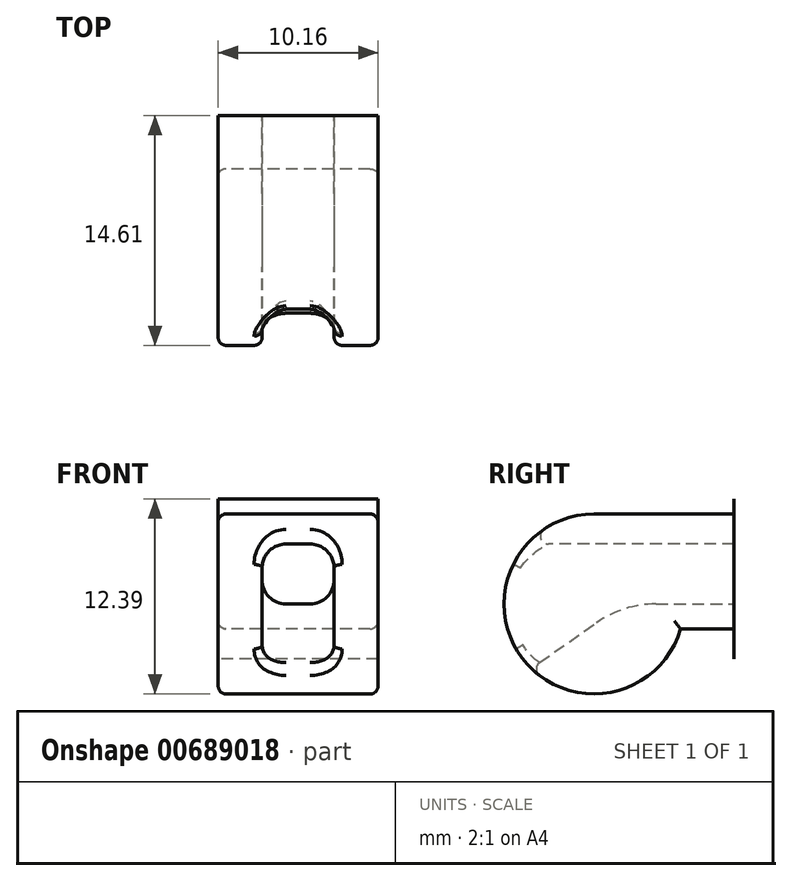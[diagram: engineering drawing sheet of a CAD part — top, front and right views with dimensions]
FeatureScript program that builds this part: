
annotation { "Feature Type Name" : "Feature", "Feature Type Description" : "" }
export const myFeature = defineFeature(function(context is Context, id is Id, definition is map)
    precondition{}
    {
        {
            var Q0;
            Q0=qCreatedBy(makeId("Front.planeOp"),FACE);
            var sketch = newSketch(context, id + "F0", { "sketchPlane" : qUnion([Q0])});
            skLineSegment(sketch, "E0.bottom", {"start": v(10.16, 8.26) * mm, "end": v(-10.16, 8.26) * mm});
            skLineSegment(sketch, "E0.top", {"start": v(10.16, -8.26) * mm, "end": v(-10.16, -8.26) * mm});
            skLineSegment(sketch, "E0.left", {"start": v(10.16, 8.26) * mm, "end": v(10.16, -8.26) * mm});
            skLineSegment(sketch, "E0.right", {"start": v(-10.16, 8.26) * mm, "end": v(-10.16, -8.26) * mm});
            skPoint(sketch, "E0.middle", {"position": v(0, 0) * mm});
            skSolve(sketch);
        }
        {
            var Q0;
            Q0=qCreatedBy(makeId("Right.planeOp"),FACE);
            var sketch = newSketch(context, id + "F1", { "sketchPlane" : qUnion([Q0])});
            skCircle(sketch, "E1", {"center": v(-8.9, 0) * mm, "radius": 5.72 * mm});
            skLineSegment(sketch, "E2", {"start": v(-8.9, 5.72) * mm, "end": v(0, 5.72) * mm});
            skLineSegment(sketch, "E3", {"start": v(-3.4, -1.59) * mm, "end": v(0, -1.59) * mm});
            skPoint(sketch, "E4.0", {"position": v(0, 8.26) * mm});
            skPoint(sketch, "E5.0", {"position": v(0, -8.26) * mm});
            skLineSegment(sketch, "E6.0", {"start": v(0, 8.26) * mm, "end": v(0, -8.26) * mm});
            skPoint(sketch, "E7", {"position": v(0, 0) * mm});
            skSolve(sketch);
        }
        {
            var Q0;
            Q0=qSketchRegion(id+"F1",true);
            extrude(context, id + "F2", {"entities" : qUnion([Q0]), "endBound" : BoundingType.SYMMETRIC, "depth" : 10.16 * mm, "offsetDistance" : 25.4 * mm});
        }
        {
            var Q0;
            Q0=makeQuery(id+"F2.opExtrude","SWEPT_FACE",FACE,{"disambiguationData":[OSD([sQuery(id+"F1.wireOp",EDGE,"E6.0")])]});
            var sketch = newSketch(context, id + "F3", { "sketchPlane" : qUnion([Q0])});
            skLineSegment(sketch, "E8.bottom", {"start": v(-5.08, 5.72) * mm, "end": v(5.08, 5.72) * mm});
            skLineSegment(sketch, "E8.top", {"start": v(-5.08, -1.59) * mm, "end": v(5.08, -1.59) * mm});
            skLineSegment(sketch, "E8.left", {"start": v(-5.08, 5.72) * mm, "end": v(-5.08, -1.59) * mm});
            skLineSegment(sketch, "E8.right", {"start": v(5.08, 5.72) * mm, "end": v(5.08, -1.59) * mm});
            skSolve(sketch);
        }
        {
            var Q0;
            Q0 = qSketchRegion(id + "F3", true);
            extrude(context, id + "F4", {"entities" : qUnion([Q0]), "operationType" : NewBodyOperationType.ADD, "depth" : 1 / 406.4 * mm, "offsetDistance" : 25.4 * mm});
        }
        {
            var Q0;
            Q0=makeQuery(id+"F4.opExtrude","CAP_FACE",FACE,{"disambiguationData":[OSD([sQuery(id+"F3.wireOp",EDGE,"E8.bottom"),sQuery(id+"F3.wireOp",EDGE,"E8.top"),sQuery(id+"F3.wireOp",EDGE,"E8.left"),sQuery(id+"F3.wireOp",EDGE,"E8.right")])],"isStart":false});
            var sketch = newSketch(context, id + "F5", { "sketchPlane" : qUnion([Q0])});
            skLineSegment(sketch, "E9.bottom", {"start": v(-5.08, 6.67) * mm, "end": v(5.08, 6.67) * mm});
            skLineSegment(sketch, "E9.top", {"start": v(-5.08, -3.5) * mm, "end": v(5.08, -3.5) * mm});
            skLineSegment(sketch, "E9.left", {"start": v(-5.08, 6.67) * mm, "end": v(-5.08, -3.5) * mm});
            skLineSegment(sketch, "E9.right", {"start": v(5.08, 6.67) * mm, "end": v(5.08, -3.5) * mm});
            skLineSegment(sketch, "E10", {"start": v(0, 0) * mm, "end": v(0, 6.67) * mm, "construction": true});
            skPoint(sketch, "E11", {"position": v(0, 6.67) * mm});
            skSolve(sketch);
        }
        {
            var Q0;
            Q0 = qSketchRegion(id + "F5", true);
            extrude(context, id + "F6", {"entities" : qUnion([Q0]), "operationType" : NewBodyOperationType.ADD, "depth" : 1 / 406.4 * mm, "offsetDistance" : 25.4 * mm});
        }
        {
            var Q0;
            Q0=makeQuery(id+"FJUqmKPQ4yw4BPf_1.boolean.opBoolean","INTERSECT",EDGE,{"derivedFrom":[makeQuery(id+"Fq8YA3T5FWs05GF_0.opExtrude","CAP_FACE",FACE,{"disambiguationData":[OSD([sQuery(id+"F0.wireOp",EDGE,"E0.bottom"),sQuery(id+"F0.wireOp",EDGE,"E0.top"),sQuery(id+"F0.wireOp",EDGE,"E0.left"),sQuery(id+"F0.wireOp",EDGE,"E0.right")])],"isStart":true}),makeQuery(id+"FJUqmKPQ4yw4BPf_1.opExtrude","SWEPT_FACE",FACE,{"disambiguationData":[OSD([sQuery(id+"FeA7wIC9zSnlyUK_1.wireOp",EDGE,"6bacabb4-34cd-4eb1-88e9-ca2e72023442.0")])]})]});
            var Q1;
            Q1=makeQuery(id+"F3S6jZqAGkzocYz_1.boolean.opBoolean","INTERSECT",EDGE,{"derivedFrom":[makeQuery(id+"FJUqmKPQ4yw4BPf_1.boolean.opBoolean","COPY",FACE,{"derivedFrom":makeQuery(id+"FJUqmKPQ4yw4BPf_1.opExtrude","CAP_FACE",FACE,{"disambiguationData":[OSD([sQuery(id+"FeA7wIC9zSnlyUK_1.wireOp",EDGE,"21b268ef-5e91-4854-b6ca-af72ce9b2bcd.0"),sQuery(id+"FeA7wIC9zSnlyUK_1.wireOp",EDGE,"6bacabb4-34cd-4eb1-88e9-ca2e72023442.0"),sQuery(id+"FeA7wIC9zSnlyUK_1.wireOp",EDGE,"vvrvkM2s-nN7P-mgGs-fwoX-CmVmCMUNgCXH"),sQuery(id+"FeA7wIC9zSnlyUK_1.wireOp",EDGE,"wpNWQAo5-k2Ei-IkE6-PnNk-Ez94kCgWJtzR")])],"isStart":false})}),makeQuery(id+"F3S6jZqAGkzocYz_1.opExtrude","SWEPT_FACE",FACE,{"disambiguationData":[OSD([sQuery(id+"FIZGDcuUzl3fkC7_1.wireOp",EDGE,"Vstx0dWy-UYXF-5Riu-W8jx-rFPZ5lrV4CEe"),sQuery(id+"FIZGDcuUzl3fkC7_1.wireOp",EDGE,"i7qXx4Os-EHyz-alrp-C85T-eEPyD9XQ6b9H")])]})]});
            var Q2;
            {var subQ0=sQuery(id+"FIZGDcuUzl3fkC7_1.wireOp",EDGE,"i7qXx4Os-EHyz-alrp-C85T-eEPyD9XQ6b9H");var subQ1=sQuery(id+"FIZGDcuUzl3fkC7_1.wireOp",EDGE,"Vstx0dWy-UYXF-5Riu-W8jx-rFPZ5lrV4CEe");var subQ2=sQuery(id+"FIZGDcuUzl3fkC7_1.wireOp",EDGE,"d3481635-f86c-41fd-ba71-1d78659e9d92.2");var subQ3=makeQuery(id+"FJUqmKPQ4yw4BPf_1.boolean.opBoolean","COPY",FACE,{"derivedFrom":makeQuery(id+"FJUqmKPQ4yw4BPf_1.opExtrude","CAP_FACE",FACE,{"disambiguationData":[OSD([sQuery(id+"FeA7wIC9zSnlyUK_1.wireOp",EDGE,"21b268ef-5e91-4854-b6ca-af72ce9b2bcd.0"),sQuery(id+"FeA7wIC9zSnlyUK_1.wireOp",EDGE,"6bacabb4-34cd-4eb1-88e9-ca2e72023442.0"),sQuery(id+"FeA7wIC9zSnlyUK_1.wireOp",EDGE,"vvrvkM2s-nN7P-mgGs-fwoX-CmVmCMUNgCXH"),sQuery(id+"FeA7wIC9zSnlyUK_1.wireOp",EDGE,"wpNWQAo5-k2Ei-IkE6-PnNk-Ez94kCgWJtzR")])],"isStart":false})});var subQ4=sQuery(id+"F0.wireOp",EDGE,"E0.right");Q2=makeQuery(id+"FDKQeK4xXi7c1Lz_1.opFillet","BLEND_EDGE",EDGE,{"blendedFrom":[makeQuery(id+"F3S6jZqAGkzocYz_1.boolean.opBoolean","COPY",EDGE,{"disambiguationData":[TD([makeQuery(id+"Fq8YA3T5FWs05GF_0.opExtrude","SWEPT_FACE",FACE,{"disambiguationData":[OSD([subQ4])]})])],"derivedFrom":makeQuery(id+"F3S6jZqAGkzocYz_1.opExtrude","SWEPT_EDGE",EDGE,{"disambiguationData":[OSD([subQ2,subQ0])]})}),makeQuery(id+"FUXpRk3uys0C6SX_1.boolean.opBoolean","MERGE",FACE,{"derivedFrom":[subQ3,makeQuery(id+"FUXpRk3uys0C6SX_1.opExtrude","CAP_FACE",FACE,{"disambiguationData":[OSD([sQuery(id+"FIZGDcuUzl3fkC7_1.wireOp",EDGE,"d3481635-f86c-41fd-ba71-1d78659e9d92.0"),sQuery(id+"FIZGDcuUzl3fkC7_1.wireOp",EDGE,"d3481635-f86c-41fd-ba71-1d78659e9d92.1"),subQ2,sQuery(id+"FIZGDcuUzl3fkC7_1.wireOp",EDGE,"d3481635-f86c-41fd-ba71-1d78659e9d92.3"),subQ1,sQuery(id+"FIZGDcuUzl3fkC7_1.wireOp",EDGE,"u2ZkYEZy-LntR-KaXa-GYHO-8ooGsvoJke9S"),subQ0])],"isStart":true})]})],"blendedInto":[makeQuery(id+"FUXpRk3uys0C6SX_1.boolean.opBoolean","MERGE",FACE,{"derivedFrom":[subQ3,makeQuery(id+"FUXpRk3uys0C6SX_1.opExtrude","CAP_FACE",FACE,{"disambiguationData":[OSD([sQuery(id+"FIZGDcuUzl3fkC7_1.wireOp",EDGE,"d3481635-f86c-41fd-ba71-1d78659e9d92.0"),sQuery(id+"FIZGDcuUzl3fkC7_1.wireOp",EDGE,"d3481635-f86c-41fd-ba71-1d78659e9d92.1"),subQ2,sQuery(id+"FIZGDcuUzl3fkC7_1.wireOp",EDGE,"d3481635-f86c-41fd-ba71-1d78659e9d92.3"),subQ1,sQuery(id+"FIZGDcuUzl3fkC7_1.wireOp",EDGE,"u2ZkYEZy-LntR-KaXa-GYHO-8ooGsvoJke9S"),subQ0])],"isStart":true})]})]});}
            var Q3;
            Q3=makeQuery(id+"FJUqmKPQ4yw4BPf_1.boolean.opBoolean","INTERSECT",EDGE,{"derivedFrom":[makeQuery(id+"Fq8YA3T5FWs05GF_0.opExtrude","CAP_FACE",FACE,{"disambiguationData":[OSD([sQuery(id+"F0.wireOp",EDGE,"E0.bottom"),sQuery(id+"F0.wireOp",EDGE,"E0.top"),sQuery(id+"F0.wireOp",EDGE,"E0.left"),sQuery(id+"F0.wireOp",EDGE,"E0.right")])],"isStart":true}),makeQuery(id+"FJUqmKPQ4yw4BPf_1.opExtrude","CAP_FACE",FACE,{"disambiguationData":[OSD([sQuery(id+"FeA7wIC9zSnlyUK_1.wireOp",EDGE,"21b268ef-5e91-4854-b6ca-af72ce9b2bcd.0"),sQuery(id+"FeA7wIC9zSnlyUK_1.wireOp",EDGE,"6bacabb4-34cd-4eb1-88e9-ca2e72023442.0"),sQuery(id+"FeA7wIC9zSnlyUK_1.wireOp",EDGE,"vvrvkM2s-nN7P-mgGs-fwoX-CmVmCMUNgCXH"),sQuery(id+"FeA7wIC9zSnlyUK_1.wireOp",EDGE,"wpNWQAo5-k2Ei-IkE6-PnNk-Ez94kCgWJtzR")])],"isStart":false})]});
            var Q4;
            Q4=makeQuery(id+"FUXpRk3uys0C6SX_1.boolean.opBoolean","COPY",EDGE,{"derivedFrom":makeQuery(id+"FUXpRk3uys0C6SX_1.opExtrude","SWEPT_EDGE",EDGE,{"disambiguationData":[OSD([sQuery(id+"FIZGDcuUzl3fkC7_1.wireOp",EDGE,"Vstx0dWy-UYXF-5Riu-W8jx-rFPZ5lrV4CEe"),sQuery(id+"FIZGDcuUzl3fkC7_1.wireOp",EDGE,"u2ZkYEZy-LntR-KaXa-GYHO-8ooGsvoJke9S"),sQuery(id+"FIZGDcuUzl3fkC7_1.wireOp",EDGE,"i7qXx4Os-EHyz-alrp-C85T-eEPyD9XQ6b9H")])]})});
            var Q5;
            Q5=makeQuery(id+"F3S6jZqAGkzocYz_1.boolean.opBoolean","INTERSECT",EDGE,{"derivedFrom":[makeQuery(id+"FJUqmKPQ4yw4BPf_1.boolean.opBoolean","COPY",FACE,{"derivedFrom":makeQuery(id+"FJUqmKPQ4yw4BPf_1.opExtrude","CAP_FACE",FACE,{"disambiguationData":[OSD([sQuery(id+"FeA7wIC9zSnlyUK_1.wireOp",EDGE,"21b268ef-5e91-4854-b6ca-af72ce9b2bcd.0"),sQuery(id+"FeA7wIC9zSnlyUK_1.wireOp",EDGE,"6bacabb4-34cd-4eb1-88e9-ca2e72023442.0"),sQuery(id+"FeA7wIC9zSnlyUK_1.wireOp",EDGE,"vvrvkM2s-nN7P-mgGs-fwoX-CmVmCMUNgCXH"),sQuery(id+"FeA7wIC9zSnlyUK_1.wireOp",EDGE,"wpNWQAo5-k2Ei-IkE6-PnNk-Ez94kCgWJtzR")])],"isStart":true})}),makeQuery(id+"F3S6jZqAGkzocYz_1.opExtrude","SWEPT_FACE",FACE,{"disambiguationData":[OSD([sQuery(id+"FIZGDcuUzl3fkC7_1.wireOp",EDGE,"Vstx0dWy-UYXF-5Riu-W8jx-rFPZ5lrV4CEe"),sQuery(id+"FIZGDcuUzl3fkC7_1.wireOp",EDGE,"i7qXx4Os-EHyz-alrp-C85T-eEPyD9XQ6b9H")])]})]});
            var Q6;
            Q6=makeQuery(id+"FJUqmKPQ4yw4BPf_1.boolean.opBoolean","INTERSECT",EDGE,{"derivedFrom":[makeQuery(id+"Fq8YA3T5FWs05GF_0.opExtrude","CAP_FACE",FACE,{"disambiguationData":[OSD([sQuery(id+"F0.wireOp",EDGE,"E0.bottom"),sQuery(id+"F0.wireOp",EDGE,"E0.top"),sQuery(id+"F0.wireOp",EDGE,"E0.left"),sQuery(id+"F0.wireOp",EDGE,"E0.right")])],"isStart":true}),makeQuery(id+"FJUqmKPQ4yw4BPf_1.opExtrude","CAP_FACE",FACE,{"disambiguationData":[OSD([sQuery(id+"FeA7wIC9zSnlyUK_1.wireOp",EDGE,"21b268ef-5e91-4854-b6ca-af72ce9b2bcd.0"),sQuery(id+"FeA7wIC9zSnlyUK_1.wireOp",EDGE,"6bacabb4-34cd-4eb1-88e9-ca2e72023442.0"),sQuery(id+"FeA7wIC9zSnlyUK_1.wireOp",EDGE,"vvrvkM2s-nN7P-mgGs-fwoX-CmVmCMUNgCXH"),sQuery(id+"FeA7wIC9zSnlyUK_1.wireOp",EDGE,"wpNWQAo5-k2Ei-IkE6-PnNk-Ez94kCgWJtzR")])],"isStart":true})]});
            var Q7;
            Q7=makeQuery(id+"F2.opExtrude","CAP_EDGE",EDGE,{"disambiguationData":[OSD([sQuery(id+"F1.wireOp",EDGE,"E2")])],"isStart":false});
            var Q8;
            Q8=makeQuery(id+"F2.opExtrude","CAP_EDGE",EDGE,{"disambiguationData":[OSD([sQuery(id+"F1.wireOp",EDGE,"E2")])],"isStart":true});
            var Q9;
            Q9=makeQuery(id+"F2.opExtrude","CAP_EDGE",EDGE,{"disambiguationData":[OSD([sQuery(id+"F1.wireOp",EDGE,"E3")])],"isStart":false});
            var Q10;
            Q10=makeQuery(id+"F2.opExtrude","CAP_EDGE",EDGE,{"disambiguationData":[OSD([sQuery(id+"F1.wireOp",EDGE,"E3")])],"isStart":true});
            fillet(context, id + "F7", {"entities" : qUnion([Q0, Q1, Q2, Q3, Q4, Q5, Q6, Q7, Q8, Q9, Q10]), "radius" : 0.5 * mm, "tangentPropagation" : true, "allowEdgeOverflow" : false});
        }
        {
            var Q0;
            Q0=qCreatedBy(makeId("Right.planeOp"),FACE);
            var sketch = newSketch(context, id + "F8", { "sketchPlane" : qUnion([Q0])});
            skLineSegment(sketch, "E12", {"start": v(3.18, 3.81) * mm, "end": v(-18.28, 3.8) * mm});
            skLineSegment(sketch, "E13", {"start": v(-18.28, 3.8) * mm, "end": v(-18.28, -7.87) * mm});
            skLineSegment(sketch, "E14", {"start": v(-18.28, -7.87) * mm, "end": v(-8.74, -1.2) * mm});
            skArc(sketch, "E15", {"start": v(-4.95, 0) * mm, "mid": v(-6.94, -0.3) * mm, "end": v(-8.74, -1.2) * mm});
            skLineSegment(sketch, "E16", {"start": v(-4.95, 0) * mm, "end": v(3.18, 0) * mm});
            skLineSegment(sketch, "E17", {"start": v(3.18, 0) * mm, "end": v(3.18, 3.81) * mm});
            skSolve(sketch);
        }
        {
            var Q0;
            Q0 = qSketchRegion(id + "F8", true);
            extrude(context, id + "F9", {"entities" : qUnion([Q0]), "operationType" : NewBodyOperationType.REMOVE, "endBound" : BoundingType.SYMMETRIC, "oppositeDirection" : true, "depth" : 4.57 * mm, "offsetDistance" : 25.4 * mm});
        }
        {
            var Q0;
            Q0=makeQuery(id+"F9.boolean.opBoolean","COPY",EDGE,{"derivedFrom":makeQuery(id+"F9.opExtrude","CAP_EDGE",EDGE,{"disambiguationData":[OSD([sQuery(id+"F8.wireOp",EDGE,"E15")])],"isStart":false})});
            var Q1;
            Q1=makeQuery(id+"F9.boolean.opBoolean","COPY",EDGE,{"derivedFrom":makeQuery(id+"F9.opExtrude","CAP_EDGE",EDGE,{"disambiguationData":[OSD([sQuery(id+"F8.wireOp",EDGE,"E12")])],"isStart":false})});
            var Q2;
            Q2=makeQuery(id+"F9.boolean.opBoolean","COPY",EDGE,{"derivedFrom":makeQuery(id+"F9.opExtrude","CAP_EDGE",EDGE,{"disambiguationData":[OSD([sQuery(id+"F8.wireOp",EDGE,"E12")])],"isStart":true})});
            var Q3;
            Q3=makeQuery(id+"F9.boolean.opBoolean","COPY",EDGE,{"derivedFrom":makeQuery(id+"F9.opExtrude","CAP_EDGE",EDGE,{"disambiguationData":[OSD([sQuery(id+"F8.wireOp",EDGE,"E15")])],"isStart":true})});
            fillet(context, id + "F10", {"entities" : qUnion([Q0, Q1, Q2, Q3]), "radius" : 1.52 * mm, "tangentPropagation" : true, "allowEdgeOverflow" : false});
        }
        {
            var Q0;
            Q0=makeQuery(id+"F9.boolean.opBoolean","INTERSECT",EDGE,{"derivedFrom":[makeQuery(id+"F2.opExtrude","SWEPT_FACE",FACE,{"disambiguationData":[OSD([sQuery(id+"F1.wireOp",EDGE,"E1")])]}),makeQuery(id+"F9.opExtrude","CAP_FACE",FACE,{"disambiguationData":[OSD([sQuery(id+"F8.wireOp",EDGE,"E12"),sQuery(id+"F8.wireOp",EDGE,"E13"),sQuery(id+"F8.wireOp",EDGE,"E14"),sQuery(id+"F8.wireOp",EDGE,"E15"),sQuery(id+"F8.wireOp",EDGE,"E16"),sQuery(id+"F8.wireOp",EDGE,"E17")])],"isStart":false})]});
            fillet(context, id + "F11", {"entities" : qUnion([Q0]), "radius" : 0.5 * mm, "tangentPropagation" : true, "allowEdgeOverflow" : false});
        }
    });
